# Revit family: SYSCOOL FLOOR 24 HP Q, внутренний блок
name_source: partatom
category: Оборудование
units: mm (PartAtom-declared; Revit-internal decimal feet)

## family parameters
Всегда вертикально = Да
Заголовок OmniClass = Climate Control (HVAC)
На основе рабочей плоскости = Нет
Номер OmniClass = 23.75.00.00
Общий = Нет
При загрузке вырезать с полостями = Нет
Размер круглого соединителя = Использовать диаметр
Тип детали = Нормальный
Точка расчета площади = Нет

## types (1)
- MFPA-24ARN1-QB6
    Air  Flow = 910/800 m3/h
    Combine = 3030 Вт
    Combine Capacity = 2732 Вт
    Cooling Capacity = 7034 Вт
    Cooling Power Input = 2425 Вт
    Depth = 315 мм
    Gas = R410A
    Gas pipe = 15.9 мм
    Heating Capacity = 7913 Вт
    Heating Power Input = 2470 Вт
    Height = 1750 мм
    Installation = Indoor installation
    Liquid pipe = 9.52 мм
    Machine material = Galvanized Steel
    Maximum Fuse Amps = 35 А
    Min cable selection (power wiring) = 4.0x3
    Minimum Circuit Amps = 18 А
    Net Weight = 38.40 кг
    Panel color = Polar white
    Power supply = 3 phase,380-415V, 50Hz
    Series = PA
    Width = 510 мм
    clearance access behind = 50 мм
    clearance access front = 2000 мм
    clearance access left = 500 мм
    clearance access right = 500 мм
    clearance access up = 300 мм
    Группа модели = MFPA-24ARN1-QB6
    Описание = Floor standing

## geometry (parser evidence)
native form markers: Sweep x1
no freeform markers — native parametric forms only
